# Revit family: DBLTD_TheSenatorGroup_OfficeChairs_Contour
name_source: partatom
category: Furniture
units: mm (PartAtom-declared; Revit-internal decimal feet)

## family parameters
Always vertical = Yes
Cut with Voids When Loaded = No
OmniClass Number = 23.40.20.00
OmniClass Title = General Furniture and Specialties
Render Appearance Source = Family Geometry
Room Calculation Point = No
Shared = Yes
Work Plane-Based = No

## types (24) — shared parameters
Assembly Code = E2020200
AssetType = Movable
Category = Pr_40_50_12_57 Office chairs
Color = Upholstery: Various.
Constituents = Frame, Seat and Back
DurationUnit = years
ExpectedLife = 5
Finish = Frame and Plastic back available in Black, Pistachio, Navy, Orange Crush or Crayon Grey. Arm Finish: Black
Keynote = Pr_40_50_12_57 Office chairs
Manufacturer = The Senator Group
ManufacturerName = The Senator Group
ManufacturerURL = https://www.allermuir.com
Material = 100% recycled Polypropylene, upholstery.
Name = Chair
ProductInformation = https://www.senator.online
Shape = Rectangular
URL = https://www.thesenatorgroup.com
Uniclass2015Code = Pr_40_50_12_57
Uniclass2015Title = Office chairs
Uniclass2015Version = Products v1.15
Version = 1
WarrantyDescription = The Senator Group warrants that its manufactured products are free from manufacturing defects - in materials or workmanship - for a period of five (5) years.
WarrantyDurationLabor = 5
WarrantyDurationParts = 5
WarrantyDurationUnit = years
WarrantyGuarantorLabor = https://www.thesenatorgroup.com
WarrantyGuarantorParts = https://www.thesenatorgroup.com
zero-valued in all types: Cost, Default Elevation

## per-type parameters (varying)
| type | Description | FrameType | Model | ModelNumber | ModelReference | NominalDepth | NominalHeight | NominalWidth | SeatHeight | SeatType | SeatingHeight | Size | Type Comments |
| Four Leg, Plastic Shell, Upholstered Seat with No Arms | Four Leg, Plastic Shell, Upholstered Seat with No Arms | Nested_DBLTD_TheSenatorGroup_OfficeChairs_Contour_4Leg | CTR101 | CTR101 | Four Leg, Plastic Shell, Upholstered Seat with No Arms | 560 mm  [stored 1.83727 ft] | 865 mm  [stored 2.83793 ft] | 530 mm  [stored 1.73885 ft] | 0 mm  [stored 0 ft] | Nested_DBLTD_TheSenatorGroup_OfficeChairs_Contour_SeatPlasticBack | 465 mm  [stored 1.52559 ft] | 865 x 560 x 530 mm | Four Leg, Plastic Shell, Upholstered Seat with No Arms |
| Barstool, Plastic Shell, Upholstered Seat with No Arms | Barstool, Plastic Shell, Upholstered Seat with No Arms | Nested_DBLTD_TheSenatorGroup_OfficeChairs_Contour_4LegHigh | CTR103 | CTR103 | Barstool, Plastic Shell, Upholstered Seat with No Arms | 590 mm  [stored 1.9357 ft] | 1180 mm  [stored 3.87139 ft] | 565 mm  [stored 1.85367 ft] | 315 mm  [stored 1.03346 ft] | Nested_DBLTD_TheSenatorGroup_OfficeChairs_Contour_SeatPlasticBack | 785 mm | 1180 x 590 x 565 mm | Barstool, Plastic Shell, Upholstered Seat with No Arms |
| Four Leg, Plastic Shell, Upholstered Seat with Arms | Four Leg, Plastic Shell, Upholstered Seat with Arms | Nested_DBLTD_TheSenatorGroup_OfficeChairs_Contour_4LegArms | CTR101A | CTR101A | Four Leg, Plastic Shell, Upholstered Seat with Arms | 560 mm  [stored 1.83727 ft] | 865 mm  [stored 2.83793 ft] | 630 mm  [stored 2.06693 ft] | 0 mm  [stored 0 ft] | Nested_DBLTD_TheSenatorGroup_OfficeChairs_Contour_SeatPlasticBack | 465 mm  [stored 1.52559 ft] | 865 x 560 x 630 mm | Four Leg, Plastic Shell, Upholstered Seat with Arms |
| Four Leg with Castors, Plastic Shell, Upholstered Seat with No Arms | Four Leg with Castors, Plastic Shell, Upholstered Seat with No Arms | Nested_DBLTD_TheSenatorGroup_OfficeChairs_Contour_4LegCastors | CTR102 | CTR102 | Four Leg with Castors, Plastic Shell, Upholstered Seat with No Arms | 560 mm  [stored 1.83727 ft] | 865 mm  [stored 2.83793 ft] | 530 mm  [stored 1.73885 ft] | 0 mm  [stored 0 ft] | Nested_DBLTD_TheSenatorGroup_OfficeChairs_Contour_SeatPlasticBack | 465 mm  [stored 1.52559 ft] | 865 x 560 x 530 mm | Four Leg with Castors, Plastic Shell, Upholstered Seat with No Arms |
| Four Leg with Castors, Plastic Shell, Upholstered Seat with Arms | Four Leg with Castors, Plastic Shell, Upholstered Seat with Arms | Nested_DBLTD_TheSenatorGroup_OfficeChairs_Contour_4LegArmsCastors | CTR10A | CTR10A | Four Leg with Castors, Plastic Shell, Upholstered Seat with Arms | 560 mm  [stored 1.83727 ft] | 865 mm  [stored 2.83793 ft] | 630 mm  [stored 2.06693 ft] | 0 mm  [stored 0 ft] | Nested_DBLTD_TheSenatorGroup_OfficeChairs_Contour_SeatPlasticBack | 465 mm  [stored 1.52559 ft] | 865 x 560 x 630 mm | Four Leg with Castors, Plastic Shell, Upholstered Seat with Arms |
| Education, Plastic Shell, Upholstered Seat | Education, Plastic Shell, Upholstered Seat | Nested_DBLTD_TheSenatorGroup_OfficeChairs_Contour_Education | CTR104A | CTR104A | Education, Plastic Shell, Upholstered Seat | 690 mm  [stored 2.26378 ft] | 865 mm  [stored 2.83793 ft] | 675 mm  [stored 2.21457 ft] | 0 mm  [stored 0 ft] | Nested_DBLTD_TheSenatorGroup_OfficeChairs_Contour_SeatPlasticBack | 465 mm  [stored 1.52559 ft] | 865 x 690 x 675 mm | Education, Plastic Shell, Upholstered Seat |
| Task Base, Plastic Shell, Upholstered Seat with No Arms | Task Base, Plastic Shell, Upholstered Seat with No Arms | Nested_DBLTD_TheSenatorGroup_OfficeChairs_Contour_Task : Without Arms | CTR105 | CTR105 | Task Base, Plastic Shell, Upholstered Seat with No Arms | 690 mm  [stored 2.26378 ft] | 750 mm  [stored 2.46063 ft] | 750 mm  [stored 2.46063 ft] | 0 mm  [stored 0 ft] | Nested_DBLTD_TheSenatorGroup_OfficeChairs_Contour_SeatPlasticBack | 465 mm  [stored 1.52559 ft] | 865 x 750 x 750 mm | Task Base, Plastic Shell, Upholstered Seat with No Arms |
| Task Base, Plastic Shell, Upholstered Seat with Arms | Task Base, Plastic Shell, Upholstered Seat with Arms | Nested_DBLTD_TheSenatorGroup_OfficeChairs_Contour_Task : Has Arms | CTR105A | CTR105A | Task Base, Plastic Shell, Upholstered Seat with Arms | 690 mm  [stored 2.26378 ft] | 750 mm  [stored 2.46063 ft] | 750 mm  [stored 2.46063 ft] | 0 mm  [stored 0 ft] | Nested_DBLTD_TheSenatorGroup_OfficeChairs_Contour_SeatPlasticBack | 465 mm  [stored 1.52559 ft] | 865 x 750 x 750 mm | Task Base, Plastic Shell, Upholstered Seat with Arms |
| Barstool, Fully Upholstered with No Arms | Barstool, Fully Upholstered with No Arms | Nested_DBLTD_TheSenatorGroup_OfficeChairs_Contour_4LegHigh | CTR203 | CTR203 | Barstool, Fully Upholstered with No Arms | 590 mm  [stored 1.9357 ft] | 1180 mm  [stored 3.87139 ft] | 565 mm  [stored 1.85367 ft] | 315 mm  [stored 1.03346 ft] | Nested_DBLTD_TheSenatorGroup_OfficeChairs_Contour_SeatUpholsteredBack | 785 mm | 1180 x 590 x 565 mm | Barstool, Fully Upholstered with No Arms |
| Education, Fully Upholstered | Education, Fully Upholstered | Nested_DBLTD_TheSenatorGroup_OfficeChairs_Contour_Education | CTR204A | CTR204A | Education, Fully Upholstered | 690 mm  [stored 2.26378 ft] | 865 mm  [stored 2.83793 ft] | 675 mm  [stored 2.21457 ft] | 0 mm  [stored 0 ft] | Nested_DBLTD_TheSenatorGroup_OfficeChairs_Contour_SeatUpholsteredBack | 465 mm  [stored 1.52559 ft] | 865 x 690 x 675 mm | Education, Fully Upholstered |
| Barstool, Fully Upholstered Removable Covers with No Arms | Barstool, Fully Upholstered Removable Covers with No Arms | Nested_DBLTD_TheSenatorGroup_OfficeChairs_Contour_4LegHigh | CTR253 | CTR253 | Barstool, Fully Upholstered Removable Covers with No Arms | 590 mm  [stored 1.9357 ft] | 1180 mm  [stored 3.87139 ft] | 565 mm  [stored 1.85367 ft] | 315 mm  [stored 1.03346 ft] | Nested_DBLTD_TheSenatorGroup_OfficeChairs_Contour_SeatRemovableBack | 785 mm | 1180 x 590 x 565 mm | Barstool, Fully Upholstered Removable Covers with No Arms |
| Education, Fully Upholstered Removable Covers | Education, Fully Upholstered Removable Covers | Nested_DBLTD_TheSenatorGroup_OfficeChairs_Contour_Education | CTR254A | CTR254A | Education, Fully Upholstered Removable Covers | 690 mm  [stored 2.26378 ft] | 865 mm  [stored 2.83793 ft] | 675 mm  [stored 2.21457 ft] | 0 mm  [stored 0 ft] | Nested_DBLTD_TheSenatorGroup_OfficeChairs_Contour_SeatRemovableBack | 465 mm  [stored 1.52559 ft] | 865 x 690 x 675 mm | Education, Fully Upholstered Removable Covers |
| Four Leg with Castors, Fully Upholstered with Arms | Four Leg with Castors, Fully Upholstered with Arms | Nested_DBLTD_TheSenatorGroup_OfficeChairs_Contour_4LegArmsCastors | CTR20A | CTR20A | Four Leg with Castors, Fully Upholstered with Arms | 560 mm  [stored 1.83727 ft] | 865 mm  [stored 2.83793 ft] | 630 mm  [stored 2.06693 ft] | 0 mm  [stored 0 ft] | Nested_DBLTD_TheSenatorGroup_OfficeChairs_Contour_SeatUpholsteredBack | 465 mm  [stored 1.52559 ft] | 865 x 560 x 630 mm | Four Leg with Castors, Fully Upholstered with Arms |
| Four Leg with Castors, Fully Upholstered Removable Covers with Arms | Four Leg with Castors, Fully Upholstered Removable Covers with Arms | Nested_DBLTD_TheSenatorGroup_OfficeChairs_Contour_4LegArmsCastors | CTR25A | CTR25A | Four Leg with Castors, Fully Upholstered Removable Covers with Arms | 560 mm  [stored 1.83727 ft] | 865 mm  [stored 2.83793 ft] | 630 mm  [stored 2.06693 ft] | 0 mm  [stored 0 ft] | Nested_DBLTD_TheSenatorGroup_OfficeChairs_Contour_SeatRemovableBack | 465 mm  [stored 1.52559 ft] | 865 x 560 x 630 mm | Four Leg with Castors, Fully Upholstered Removable Covers with Arms |
| Four Leg with Castors, Fully Upholstered with No Arms | Four Leg with Castors, Fully Upholstered with No Arms | Nested_DBLTD_TheSenatorGroup_OfficeChairs_Contour_4LegCastors | CTR202 | CTR202 | Four Leg with Castors, Fully Upholstered with No Arms | 560 mm  [stored 1.83727 ft] | 865 mm  [stored 2.83793 ft] | 530 mm  [stored 1.73885 ft] | 0 mm  [stored 0 ft] | Nested_DBLTD_TheSenatorGroup_OfficeChairs_Contour_SeatUpholsteredBack | 465 mm  [stored 1.52559 ft] | 865 x 560 x 530 mm | Four Leg with Castors, Fully Upholstered with No Arms |
| Four Leg with Castors, Fully Upholstered Removable Covers with No Arms | Four Leg with Castors, Fully Upholstered with No Arms | Nested_DBLTD_TheSenatorGroup_OfficeChairs_Contour_4LegCastors | CTR225 | CTR225 | Four Leg with Castors, Fully Upholstered with No Arms | 560 mm  [stored 1.83727 ft] | 865 mm  [stored 2.83793 ft] | 530 mm  [stored 1.73885 ft] | 0 mm  [stored 0 ft] | Nested_DBLTD_TheSenatorGroup_OfficeChairs_Contour_SeatRemovableBack | 465 mm  [stored 1.52559 ft] | 865 x 560 x 530 mm | Four Leg with Castors, Fully Upholstered with No Arms |
| Four Leg, Fully Upholstered with Arms | Four Leg, Fully Upholstered with Arms | Nested_DBLTD_TheSenatorGroup_OfficeChairs_Contour_4LegArms | CTR201A | CTR201A | Four Leg, Fully Upholstered with Arms | 560 mm  [stored 1.83727 ft] | 865 mm  [stored 2.83793 ft] | 630 mm  [stored 2.06693 ft] | 0 mm  [stored 0 ft] | Nested_DBLTD_TheSenatorGroup_OfficeChairs_Contour_SeatUpholsteredBack | 465 mm  [stored 1.52559 ft] | 865 x 560 x 630 mm | Four Leg, Fully Upholstered with Arms |
| Four Leg, Fully Upholstered Removable Covers with Arms | Four Leg, Fully Upholstered Removable Covers with Arms | Nested_DBLTD_TheSenatorGroup_OfficeChairs_Contour_4LegArms | CTR251A | CTR251A | Four Leg, Fully Upholstered Removable Covers with Arms | 560 mm  [stored 1.83727 ft] | 865 mm  [stored 2.83793 ft] | 630 mm  [stored 2.06693 ft] | 0 mm  [stored 0 ft] | Nested_DBLTD_TheSenatorGroup_OfficeChairs_Contour_SeatRemovableBack | 465 mm  [stored 1.52559 ft] | 865 x 560 x 630 mm | Four Leg, Fully Upholstered Removable Covers with Arms |
| Four Leg, Fully Upholstered with No Arms | Four Leg, Fully Upholstered with No Arms | Nested_DBLTD_TheSenatorGroup_OfficeChairs_Contour_4Leg | CTR201 | CTR201 | Four Leg, Fully Upholstered with No Arms | 560 mm  [stored 1.83727 ft] | 865 mm  [stored 2.83793 ft] | 530 mm  [stored 1.73885 ft] | 0 mm  [stored 0 ft] | Nested_DBLTD_TheSenatorGroup_OfficeChairs_Contour_SeatUpholsteredBack | 465 mm  [stored 1.52559 ft] | 865 x 560 x 530 mm | Four Leg, Fully Upholstered with No Arms |
| Four Leg, Fully Upholstered Removable Covers with No Arms | Four Leg, Fully Upholstered Removable Covers with No Arms | Nested_DBLTD_TheSenatorGroup_OfficeChairs_Contour_4Leg | CTR251 | CTR251 | Four Leg, Fully Upholstered Removable Covers with No Arms | 560 mm  [stored 1.83727 ft] | 865 mm  [stored 2.83793 ft] | 530 mm  [stored 1.73885 ft] | 0 mm  [stored 0 ft] | Nested_DBLTD_TheSenatorGroup_OfficeChairs_Contour_SeatRemovableBack | 465 mm  [stored 1.52559 ft] | 865 x 560 x 530 mm | Four Leg, Fully Upholstered Removable Covers with No Arms |
| Task Base, Fully Upholstered with Arms | Task Base, Fully Upholstered with Arms | Nested_DBLTD_TheSenatorGroup_OfficeChairs_Contour_Task : Has Arms | CTR205A | CTR205A | Task Base, Fully Upholstered with Arms | 690 mm  [stored 2.26378 ft] | 750 mm  [stored 2.46063 ft] | 750 mm  [stored 2.46063 ft] | 0 mm  [stored 0 ft] | Nested_DBLTD_TheSenatorGroup_OfficeChairs_Contour_SeatUpholsteredBack | 465 mm  [stored 1.52559 ft] | 865 x 750 x 750 mm | Task Base, Fully Upholstered with Arms |
| Task Base, Fully Upholstered Removable Covers with Arms | Task Base, Fully Upholstered Removable Covers with Arms | Nested_DBLTD_TheSenatorGroup_OfficeChairs_Contour_Task : Has Arms | CTR255A | CTR255A | Task Base, Fully Upholstered Removable Covers with Arms | 690 mm  [stored 2.26378 ft] | 750 mm  [stored 2.46063 ft] | 750 mm  [stored 2.46063 ft] | 0 mm  [stored 0 ft] | Nested_DBLTD_TheSenatorGroup_OfficeChairs_Contour_SeatRemovableBack | 465 mm  [stored 1.52559 ft] | 865 x 750 x 750 mm | Task Base, Fully Upholstered Removable Covers with Arms |
| Task Base, Fully Upholstered with No Arms | Task Base, Fully Upholstered with No Arms | Nested_DBLTD_TheSenatorGroup_OfficeChairs_Contour_Task : Without Arms | CTR205 | CTR205 | Task Base, Fully Upholstered with No Arms | 690 mm  [stored 2.26378 ft] | 750 mm  [stored 2.46063 ft] | 750 mm  [stored 2.46063 ft] | 0 mm  [stored 0 ft] | Nested_DBLTD_TheSenatorGroup_OfficeChairs_Contour_SeatUpholsteredBack | 465 mm  [stored 1.52559 ft] | 865 x 750 x 750 mm | Task Base, Fully Upholstered with No Arms |
| Task Base, Fully Upholstered Removable Covers with No Arms | Task Base, Fully Upholstered Removable Covers with No Arms | Nested_DBLTD_TheSenatorGroup_OfficeChairs_Contour_Task : Without Arms | CTR255 | CTR255 | Task Base, Fully Upholstered Removable Covers with No Arms | 690 mm  [stored 2.26378 ft] | 750 mm  [stored 2.46063 ft] | 750 mm  [stored 2.46063 ft] | 0 mm  [stored 0 ft] | Nested_DBLTD_TheSenatorGroup_OfficeChairs_Contour_SeatRemovableBack | 465 mm  [stored 1.52559 ft] | 865 x 750 x 750 mm | Task Base, Fully Upholstered Removable Covers with No Arms |

note: [stored X ft] marks values corroborated as IEEE doubles in the binary element streams (Revit-internal decimal feet)

## geometry (parser evidence)
native form markers: Sweep x31
no freeform markers — native parametric forms only
